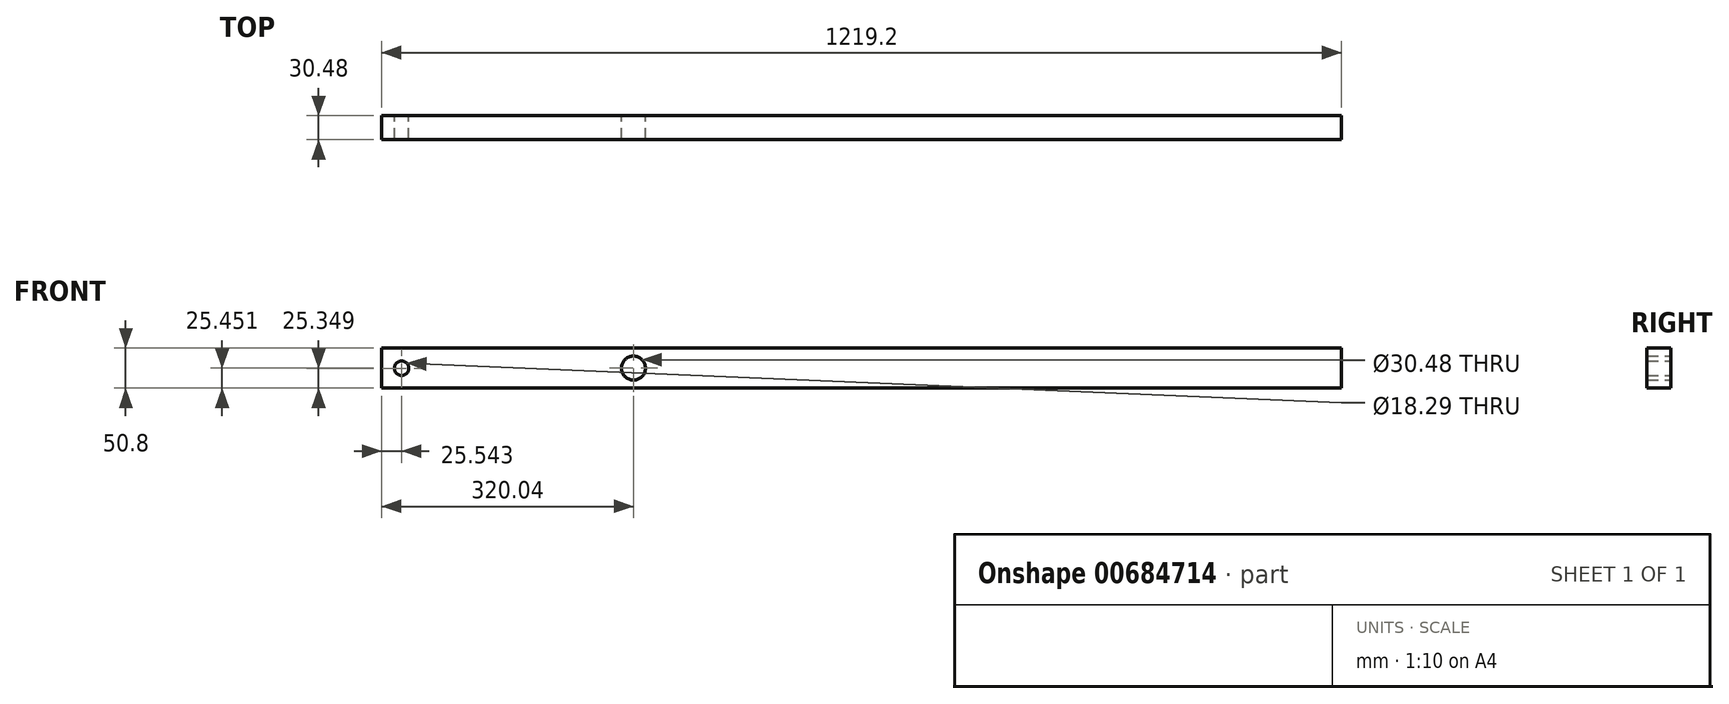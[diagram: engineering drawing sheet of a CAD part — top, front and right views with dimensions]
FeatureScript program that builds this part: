
annotation { "Feature Type Name" : "Feature", "Feature Type Description" : "" }
export const myFeature = defineFeature(function(context is Context, id is Id, definition is map)
    precondition{}
    {
        {
            var Q0;
            Q0=qCreatedBy(makeId("Front.planeOp"),FACE);
            var sketch = newSketch(context, id + "F0", { "sketchPlane" : qUnion([Q0])});
            skLineSegment(sketch, "E0", {"start": v(0, 0) * mm, "end": v(1219.2, 0) * mm});
            skLineSegment(sketch, "E1", {"start": v(1219.2, 0) * mm, "end": v(1219.2, -50.8) * mm});
            skLineSegment(sketch, "E2", {"start": v(1219.2, -50.8) * mm, "end": v(0, -50.8) * mm});
            skLineSegment(sketch, "E3", {"start": v(0, -50.8) * mm, "end": v(0, 0) * mm});
            skCircle(sketch, "E4", {"center": v(320.04, -25.35) * mm, "radius": 15.24 * mm});
            skCircle(sketch, "E5", {"center": v(25.54, -25.45) * mm, "radius": 9.14 * mm});
            skSolve(sketch);
        }
        {
            var Q0;
            Q0=makeQuery(id+"F0.imprint","IMPRINT",FACE,{"disambiguationData":[TD([[makeQuery(id+"F0.imprint","IMPRINT",EDGE,{"derivedFrom":sQuery(id+"F0.wireOp",EDGE,"E0")}),-1.0]])]});
            extrude(context, id + "F1", {"entities" : qUnion([Q0]), "depth" : 30.48 * mm, "offsetDistance" : 30.48 * mm});
        }
        {
            var Q0;
            Q0 = qSketchRegion(id + "F0", true);
            extrude(context, id + "F2", {"entities" : qUnion([Q0]), "operationType" : NewBodyOperationType.ADD, "depth" : 30.48 * mm, "offsetDistance" : 30.48 * mm});
        }
        {
            var Q0;
            Q0 = qSketchRegion(id + "F0", true);
            extrude(context, id + "F3", {"entities" : qUnion([Q0]), "operationType" : NewBodyOperationType.ADD, "depth" : 30.48 * mm, "offsetDistance" : 30.48 * mm});
        }
        {
            var Q0;
            Q0 = qSketchRegion(id + "F0", true);
            extrude(context, id + "F4", {"entities" : qUnion([Q0]), "operationType" : NewBodyOperationType.ADD, "depth" : 30.48 * mm, "offsetDistance" : 30.48 * mm});
        }
    });
